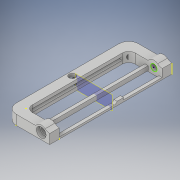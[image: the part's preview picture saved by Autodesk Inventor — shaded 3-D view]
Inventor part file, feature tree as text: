
AUTODESK INVENTOR PART (.ipt)
format: ipt  version: 2018 (Build 220112000, 112)  size: 497,152 bytes
history: native  units: in
note: dims shown in document units (in); Inventor stores cm internally (conversion verified against a paired STEP export)
features: sketch x27, extrude x17, fillet x7, hole x2, plane x1, mirror x1
ambient origin geometry x8: Origin, YZ Plane, XZ Plane, XY Plane, X Axis, Y Axis, Z Axis, Center Point
bodies: Solid1 (feature_tree)
feature tree (55):
  extrude  "Extrusion1"  Depth=0.375in
  sketch  "Sketch2"  dims[d3=0.375in d4=0.5in d5=0.375in d6=0.0in]
  extrude  "Extrusion2"  Depth=0.375in
  fillet  "Fillet1"  Radius=0.375in
  extrude  "Extrusion3"  Depth=0.375in
  extrude  "Extrusion4"  Depth=0.25in
  plane  "Work Plane1"
  mirror  "Mirror1"
  fillet  "Fillet2"  Radius=0.24in
  extrude  "Extrusion5"  Depth=0.375in
  sketch  "Sketch6"  dims[d17=1.0in d18=0.0in d19=0.24in d20=0.0in]
  extrude  "Extrusion6"  Depth=0.24in TaperAngle=0.0deg
  extrude  "Extrusion7"  Depth=0.375in
  fillet  "Fillet3"  Radius=0.25in
  fillet  "Fillet4"  Radius=0.375in
  fillet  "Fillet5"  Radius=0.25in
  fillet  "Fillet6"  Radius=0.125in
  sketch  "Sketch9"  dims[d30=0.125in d31=0.125in]
  extrude  "Extrusion8"  Depth=0.035in
  sketch  "Sketch11"  dims[d35=0.2in]
  sketch  "Sketch12"  dims[d36=0.2in d37=0.75in d38=0.375in d39=0.25in d40=0.5635in d41=0.35in d42=0.0in]
  hole  "Hole1"  [1 undecoded]
  hole  "Hole2"  [1 undecoded]
  sketch  "Sketch14"  dims[d51=3.5in d52=0.375in d53=0.0in]
  extrude  "Extrusion9"  Depth=0.125in
  sketch  "Sketch16"  dims[d58=0.4375in d59=0.0in d60=0.0625in d61=0.0in]
  extrude  "Extrusion10"  Depth=0.375in TaperAngle=0.0deg
  extrude  "Extrusion11"  Depth=0.25in
  extrude  "Extrusion12"  Depth=0.0625in TaperAngle=0.0deg
  sketch  "Sketch20"  dims[d72=0.375in d73=0.0in d74=0.4375in d75=0.0in]
  sketch  "Sketch21"  dims[d76=0.25in d77=0.4375in d78=0.0in]
  sketch  "Sketch22"
  extrude  "Extrusion13"  Depth=0.125in
  extrude  "Extrusion14"  Depth=0.25in TaperAngle=0.0deg
  fillet  "Fillet7"  Radius=0.25in
  extrude  "Extrusion15"  Depth=0.125in
  extrude  "Extrusion16"  Depth=0.4375in TaperAngle=0.0deg
  extrude  "Extrusion17"  Depth=0.4375in TaperAngle=0.0deg
  sketch  "Sketch1"  dims[d0=1.3in d1=0.375in]
  sketch  "Sketch3"  dims[d7=0.375in d8=0.0in d9=0.375in]
  sketch  "Sketch4"  dims[d10=0.24in d11=0.0in d12=0.25in d13=0.24in d14=0.0in]
  sketch  "Sketch5"  dims[d15=2.0in d16=0.375in]
  sketch  "Sketch7"  dims[d21=0.375in d22=0.0in d23=0.375in d24=0.25in d25=0.375in d26=0.25in d27=0.125in]
  sketch  "Sketch8"  dims[d28=0.035in d29=0.035in]
  sketch  "Sketch10"  dims[d32=4.375in d33=0.0in d34=0.2in]
  sketch  "Sketch13"  dims[d43=0.2in d44=0.75in d45=0.375in d46=0.25in d47=0.5635in d48=0.35in d49=0.0in d50=0.125in]
  sketch  "Sketch15"  dims[d56=0.25in d57=0.25in]
  sketch  "Sketch17"  dims[d62=0.04in d63=0.0in d64=0.125in]
  sketch  "Sketch18"  dims[d65=0.075in d66=4.04in d67=0.0in d68=0.25in]
  sketch  "Sketch19"  dims[d69=0.075in d70=0.0in d71=0.125in]
  sketch  "Sketch23"
  sketch  "Sketch24"
  sketch  "Sketch25"
  sketch  "Sketch26"
  sketch  "Sketch27"
note: 2 required parameter values undecoded (feature->parameter linkage not recoverable at this tier; creation-order binding heuristic only, values carry confidence <= 0.55)
